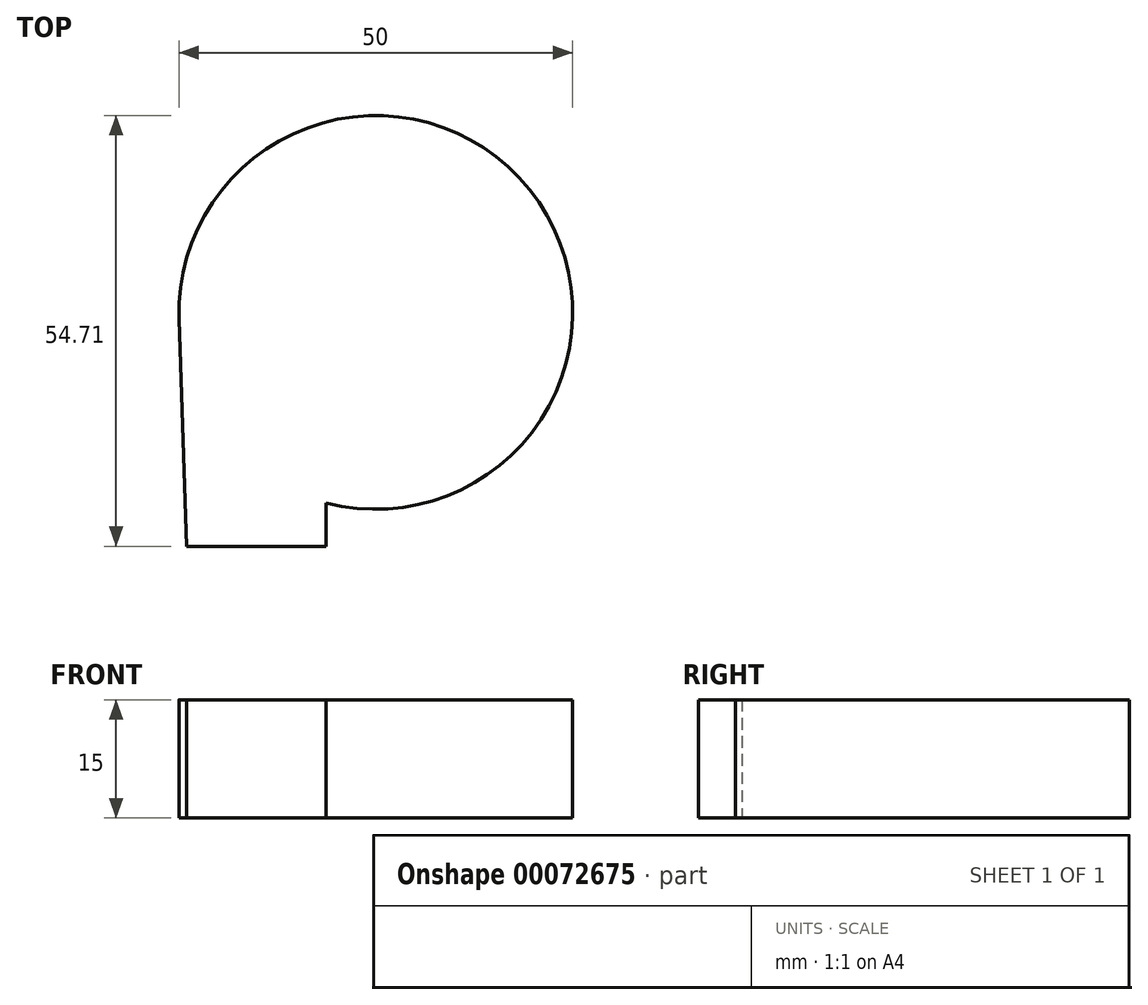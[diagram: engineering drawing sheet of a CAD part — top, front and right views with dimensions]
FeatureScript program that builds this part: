
annotation { "Feature Type Name" : "Feature", "Feature Type Description" : "" }
export const myFeature = defineFeature(function(context is Context, id is Id, definition is map)
    precondition{}
    {
        {
            var Q0;
            Q0=qCreatedBy(makeId("Top.planeOp"),FACE);
            var sketch = newSketch(context, id + "F0", { "sketchPlane" : qUnion([Q0])});
            skArc(sketch, "E0", {"start": v(-6.29, -24.2) * mm, "mid": v(19.52, 15.62) * mm, "end": v(-24.99, -0.83) * mm});
            skLineSegment(sketch, "E1", {"start": v(-6.29, -24.2) * mm, "end": v(-6.29, -29.7) * mm});
            skLineSegment(sketch, "E2", {"start": v(-6.29, -29.7) * mm, "end": v(-24.02, -29.7) * mm});
            skLineSegment(sketch, "E3", {"start": v(-24.02, -29.7) * mm, "end": v(-24.99, -0.83) * mm});
            skSolve(sketch);
        }
        {
            var Q0;
            Q0=makeQuery(id+"F0.imprint","IMPRINT",FACE,{"disambiguationData":[TD([[makeQuery(id+"F0.imprint","IMPRINT",EDGE,{"derivedFrom":sQuery(id+"F0.wireOp",EDGE,"E0")}),1.0]])]});
            extrude(context, id + "F1", {"entities" : qUnion([Q0]), "depth" : 15 * mm});
        }
    });
